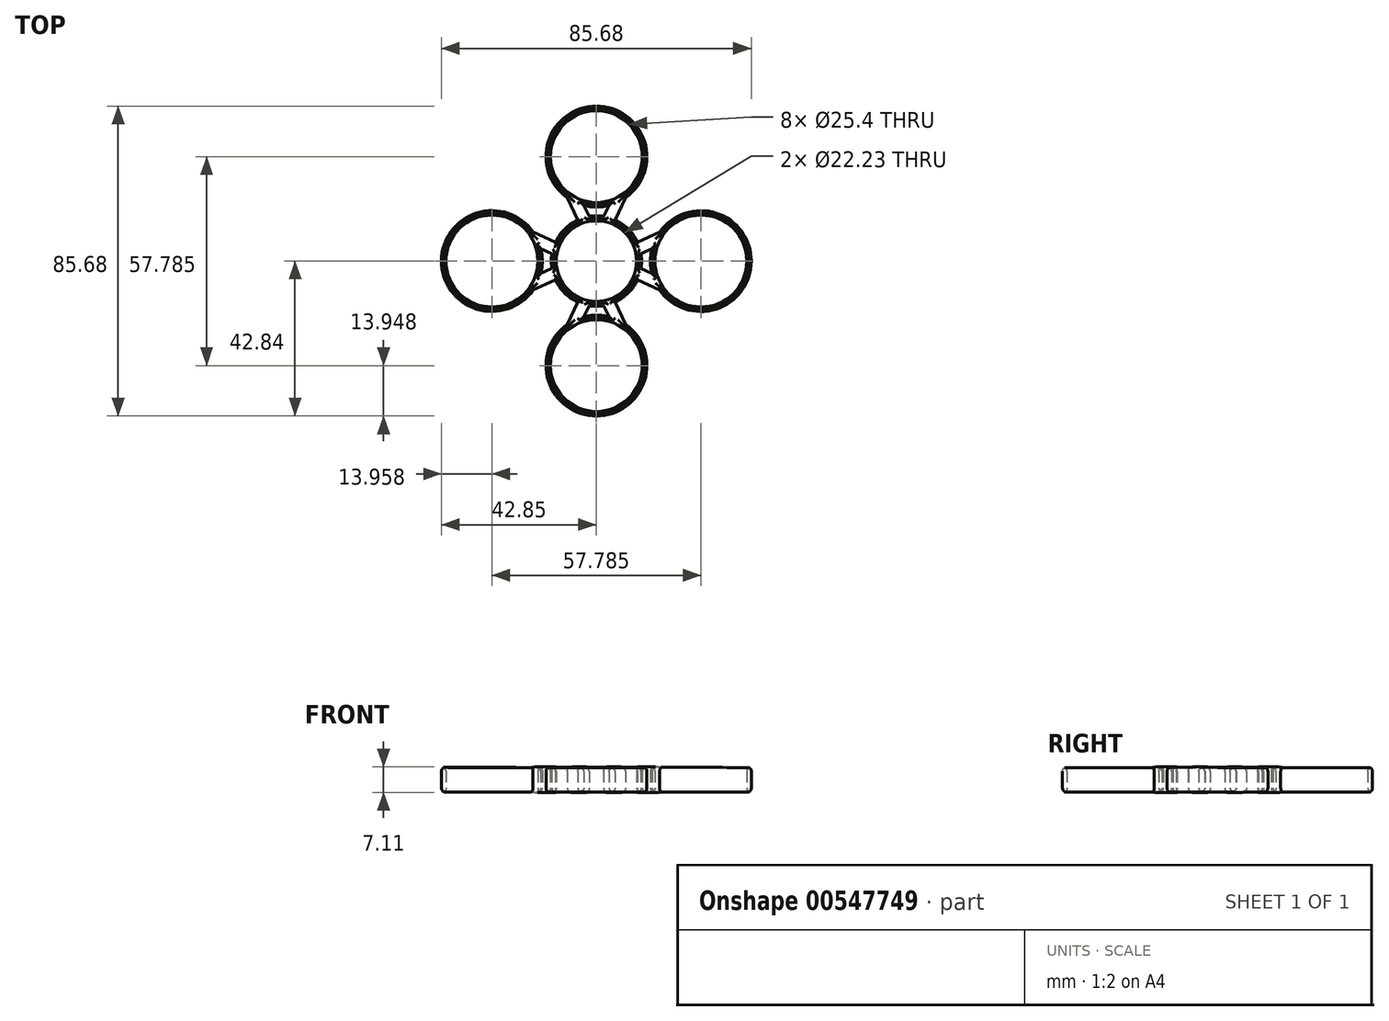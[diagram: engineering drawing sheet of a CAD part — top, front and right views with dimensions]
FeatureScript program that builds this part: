
annotation { "Feature Type Name" : "Feature", "Feature Type Description" : "" }
export const myFeature = defineFeature(function(context is Context, id is Id, definition is map)
    precondition{}
    {
        {
            var Q0;
            Q0=qCreatedBy(makeId("Top.planeOp"),FACE);
            var sketch = newSketch(context, id + "F0", { "sketchPlane" : qUnion([Q0])});
            skCircle(sketch, "E0", {"center": v(0, 0) * mm, "radius": 11.11 * mm});
            skCircle(sketch, "E1", {"center": v(0, 28.9) * mm, "radius": 12.7 * mm});
            skCircle(sketch, "E2", {"center": v(-28.9, 0) * mm, "radius": 12.7 * mm});
            skCircle(sketch, "E3", {"center": v(0, -28.9) * mm, "radius": 12.7 * mm});
            skCircle(sketch, "E4", {"center": v(28.9, 0) * mm, "radius": 12.7 * mm});
            skLineSegment(sketch, "E5", {"start": v(-8.04, 17.49) * mm, "end": v(-5.16, 11.36) * mm});
            skLineSegment(sketch, "E6", {"start": v(-3.46, 15.38) * mm, "end": v(-2.02, 12.31) * mm});
            skLineSegment(sketch, "E7.MirrorCS", {"start": v(3.46, 15.38) * mm, "end": v(2.02, 12.31) * mm});
            skLineSegment(sketch, "E8.MirrorCS", {"start": v(8.04, 17.49) * mm, "end": v(5.16, 11.36) * mm});
            skLineSegment(sketch, "E9.MirrorCS", {"start": v(8.04, -17.49) * mm, "end": v(5.16, -11.36) * mm});
            skLineSegment(sketch, "E10.MirrorCS", {"start": v(3.46, -15.38) * mm, "end": v(2.02, -12.31) * mm});
            skLineSegment(sketch, "E11.MirrorCS", {"start": v(-3.46, -15.38) * mm, "end": v(-2.02, -12.31) * mm});
            skLineSegment(sketch, "E12.MirrorCS", {"start": v(-8.04, -17.49) * mm, "end": v(-5.16, -11.36) * mm});
            skLineSegment(sketch, "E13.MirrorCS", {"start": v(17.5, 8.06) * mm, "end": v(11.36, 5.18) * mm});
            skLineSegment(sketch, "E14.MirrorCS", {"start": v(15.38, 3.47) * mm, "end": v(12.31, 2.04) * mm});
            skLineSegment(sketch, "E15.MirrorCS", {"start": v(15.36, -3.45) * mm, "end": v(12.31, -2.02) * mm});
            skLineSegment(sketch, "E16.MirrorCS", {"start": v(17.46, -8.02) * mm, "end": v(11.36, -5.16) * mm});
            skLineSegment(sketch, "E17.MirrorCS", {"start": v(-20.31, 9.35) * mm, "end": v(-20.27, 9.33) * mm});
            skLineSegment(sketch, "E18.MirrorCS", {"start": v(-16.9, 4.16) * mm, "end": v(-16.9, 4.16) * mm});
            skLineSegment(sketch, "E19.MirrorCS", {"start": v(-16.9, -4.18) * mm, "end": v(-16.9, -4.18) * mm});
            skLineSegment(sketch, "E20.MirrorCS", {"start": v(-20.31, -9.36) * mm, "end": v(-20.3, -9.36) * mm});
            skLineSegment(sketch, "E21", {"start": v(16.89, 4.18) * mm, "end": v(16.9, 4.2) * mm});
            skLineSegment(sketch, "E22", {"start": v(20.3, 9.36) * mm, "end": v(20.36, 9.4) * mm});
            skLineSegment(sketch, "E23", {"start": v(16.89, -4.16) * mm, "end": v(16.9, -4.17) * mm});
            skLineSegment(sketch, "E24", {"start": v(20.29, -9.34) * mm, "end": v(20.32, -9.37) * mm});
            skLineSegment(sketch, "E25", {"start": v(-10.13, 4.57) * mm, "end": v(-10.13, 4.57) * mm});
            skLineSegment(sketch, "E26", {"start": v(-11.03, 1.4) * mm, "end": v(-11.02, 1.4) * mm});
            skLineSegment(sketch, "E27", {"start": v(-11.03, -1.43) * mm, "end": v(-11.02, -1.42) * mm});
            skLineSegment(sketch, "E28", {"start": v(-10.13, -4.6) * mm, "end": v(-10.12, -4.58) * mm});
            skArc(sketch, "E29", {"start": v(-3.46, 15.38) * mm, "mid": v(0, 14.94) * mm, "end": v(3.46, 15.38) * mm});
            skArc(sketch, "E30.MirrorC", {"start": v(-3.46, -15.38) * mm, "mid": v(0, -14.94) * mm, "end": v(3.46, -15.38) * mm});
            skArc(sketch, "E31.MirrorC", {"start": v(-15.4, -3.47) * mm, "mid": v(-14.95, -0.01) * mm, "end": v(-15.38, 3.45) * mm});
            skArc(sketch, "E32.MirrorC", {"start": v(15.38, 3.47) * mm, "mid": v(14.93, 0.01) * mm, "end": v(15.36, -3.45) * mm});
            skPoint(sketch, "E33.orphan", {"position": v(-9.35, 20.3) * mm});
            skPoint(sketch, "E34.orphan", {"position": v(-4.17, 16.9) * mm});
            skPoint(sketch, "E35.orphan", {"position": v(4.17, 16.9) * mm});
            skPoint(sketch, "E36.orphan", {"position": v(9.35, 20.3) * mm});
            skLineSegment(sketch, "E37.trimOffspring", {"start": v(-17.48, 8.02) * mm, "end": v(-11.37, 5.15) * mm});
            skLineSegment(sketch, "E38.trimOffspring", {"start": v(-15.38, 3.45) * mm, "end": v(-12.32, 2.01) * mm});
            skLineSegment(sketch, "E39.trimOffspring", {"start": v(-15.4, -3.47) * mm, "end": v(-12.31, -2.03) * mm});
            skLineSegment(sketch, "E40.trimOffspring", {"start": v(-17.52, -8.06) * mm, "end": v(-11.36, -5.17) * mm});
            skArc(sketch, "E41.trimOffspring", {"start": v(-17.48, 8.02) * mm, "mid": v(-42.85, 0.05) * mm, "end": v(-17.52, -8.06) * mm});
            skArc(sketch, "E42.trimOffspring", {"start": v(8.04, 17.49) * mm, "mid": v(0, 42.84) * mm, "end": v(-8.04, 17.49) * mm});
            skArc(sketch, "E43.trimOffspring", {"start": v(17.46, -8.02) * mm, "mid": v(42.83, -0.05) * mm, "end": v(17.5, 8.06) * mm});
            skPoint(sketch, "E44.orphan", {"position": v(-9.35, -20.3) * mm});
            skPoint(sketch, "E45.orphan", {"position": v(-4.17, -16.9) * mm});
            skArc(sketch, "E46.trimOffspring", {"start": v(8.04, -17.49) * mm, "mid": v(0, -42.84) * mm, "end": v(-8.04, -17.49) * mm});
            skPoint(sketch, "E47.orphan", {"position": v(4.17, -16.9) * mm});
            skPoint(sketch, "E48.orphan", {"position": v(9.35, -20.3) * mm});
            skArc(sketch, "E49", {"start": v(-5.16, 11.36) * mm, "mid": v(-8.83, 8.82) * mm, "end": v(-11.37, 5.15) * mm});
            skPoint(sketch, "E50.orphan", {"position": v(-4.58, 10.12) * mm});
            skPoint(sketch, "E51.orphan", {"position": v(-1.42, 11.02) * mm});
            skArc(sketch, "E52.trimOffspring", {"start": v(2.02, 12.31) * mm, "mid": v(0, 12.48) * mm, "end": v(-2.02, 12.31) * mm});
            skPoint(sketch, "E53.orphan", {"position": v(1.42, 11.02) * mm});
            skPoint(sketch, "E54.orphan", {"position": v(4.58, 10.12) * mm});
            skArc(sketch, "E55.trimOffspring", {"start": v(-12.32, 2.01) * mm, "mid": v(-12.48, 0) * mm, "end": v(-12.31, -2.03) * mm});
            skArc(sketch, "E56.trimOffspring", {"start": v(-11.36, -5.17) * mm, "mid": v(-8.82, -8.83) * mm, "end": v(-5.16, -11.36) * mm});
            skPoint(sketch, "E57.orphan", {"position": v(-4.58, -10.12) * mm});
            skPoint(sketch, "E58.orphan", {"position": v(-1.42, -11.02) * mm});
            skArc(sketch, "E59.trimOffspring", {"start": v(-2.02, -12.31) * mm, "mid": v(0, -12.48) * mm, "end": v(2.02, -12.31) * mm});
            skPoint(sketch, "E60.orphan", {"position": v(1.42, -11.02) * mm});
            skArc(sketch, "E61.trimOffspring", {"start": v(5.16, -11.36) * mm, "mid": v(8.83, -8.82) * mm, "end": v(11.36, -5.16) * mm});
            skPoint(sketch, "E62.orphan", {"position": v(4.58, -10.12) * mm});
            skArc(sketch, "E63.trimOffspring", {"start": v(12.31, -2.02) * mm, "mid": v(12.48, 0) * mm, "end": v(12.31, 2.04) * mm});
            skLineSegment(sketch, "E64.trimOffspring", {"start": v(11.02, -1.41) * mm, "end": v(11.01, -1.4) * mm});
            skLineSegment(sketch, "E65.trimOffspring", {"start": v(10.13, -4.58) * mm, "end": v(10.11, -4.57) * mm});
            skLineSegment(sketch, "E66.trimOffspring", {"start": v(11.02, 1.43) * mm, "end": v(11.01, 1.43) * mm});
            skLineSegment(sketch, "E67.trimOffspring", {"start": v(10.12, 4.6) * mm, "end": v(10.11, 4.6) * mm});
            skArc(sketch, "E68.trimOffspring", {"start": v(11.36, 5.18) * mm, "mid": v(8.82, 8.83) * mm, "end": v(5.16, 11.36) * mm});
            skLineSegment(sketch, "E69.trimOffspring", {"start": v(0, 0.01) * mm, "end": v(0, 0) * mm});
            skLineSegment(sketch, "E70.trimOffspring", {"start": v(-0.01, 0) * mm, "end": v(0, 0) * mm});
            skLineSegment(sketch, "E71.trimOffspring", {"start": v(-0.01, 0) * mm, "end": v(-0.01, 0) * mm});
            skLineSegment(sketch, "E72.trimOffspring", {"start": v(0, 0) * mm, "end": v(-0.01, 0) * mm});
            skSolve(sketch);
        }
        {
            var Q0;
            Q0=makeQuery(id+"F0.imprint","IMPRINT",FACE,{"disambiguationData":[TD([[makeQuery(id+"F0.imprint","IMPRINT",EDGE,{"derivedFrom":sQuery(id+"F0.wireOp",EDGE,"E1")}),-1.0]])]});
            extrude(context, id + "F1", {"entities" : qUnion([Q0]), "depth" : 7.11 * mm, "offsetDistance" : 25.4 * mm});
        }
        {
            var Q0;
            Q0=makeQuery(id+"F1.opExtrude","CAP_FACE",FACE,{"disambiguationData":[OSD([sQuery(id+"F0.wireOp",EDGE,"E0"),sQuery(id+"F0.wireOp",EDGE,"E1"),sQuery(id+"F0.wireOp",EDGE,"E2"),sQuery(id+"F0.wireOp",EDGE,"E3"),sQuery(id+"F0.wireOp",EDGE,"E4"),sQuery(id+"F0.wireOp",EDGE,"E5"),sQuery(id+"F0.wireOp",EDGE,"E6"),sQuery(id+"F0.wireOp",EDGE,"E7.MirrorCS"),sQuery(id+"F0.wireOp",EDGE,"E8.MirrorCS"),sQuery(id+"F0.wireOp",EDGE,"E9.MirrorCS"),sQuery(id+"F0.wireOp",EDGE,"E10.MirrorCS"),sQuery(id+"F0.wireOp",EDGE,"E11.MirrorCS"),sQuery(id+"F0.wireOp",EDGE,"E12.MirrorCS"),sQuery(id+"F0.wireOp",EDGE,"E13.MirrorCS"),sQuery(id+"F0.wireOp",EDGE,"E14.MirrorCS"),sQuery(id+"F0.wireOp",EDGE,"E15.MirrorCS"),sQuery(id+"F0.wireOp",EDGE,"E16.MirrorCS"),sQuery(id+"F0.wireOp",EDGE,"E29"),sQuery(id+"F0.wireOp",EDGE,"E30.MirrorC"),sQuery(id+"F0.wireOp",EDGE,"E31.MirrorC"),sQuery(id+"F0.wireOp",EDGE,"E32.MirrorC"),sQuery(id+"F0.wireOp",EDGE,"E37.trimOffspring"),sQuery(id+"F0.wireOp",EDGE,"E38.trimOffspring"),sQuery(id+"F0.wireOp",EDGE,"E39.trimOffspring"),sQuery(id+"F0.wireOp",EDGE,"E40.trimOffspring"),sQuery(id+"F0.wireOp",EDGE,"E41.trimOffspring"),sQuery(id+"F0.wireOp",EDGE,"E42.trimOffspring"),sQuery(id+"F0.wireOp",EDGE,"E43.trimOffspring"),sQuery(id+"F0.wireOp",EDGE,"E46.trimOffspring"),sQuery(id+"F0.wireOp",EDGE,"E49"),sQuery(id+"F0.wireOp",EDGE,"E52.trimOffspring"),sQuery(id+"F0.wireOp",EDGE,"E55.trimOffspring"),sQuery(id+"F0.wireOp",EDGE,"E56.trimOffspring"),sQuery(id+"F0.wireOp",EDGE,"E59.trimOffspring"),sQuery(id+"F0.wireOp",EDGE,"E61.trimOffspring"),sQuery(id+"F0.wireOp",EDGE,"E63.trimOffspring"),sQuery(id+"F0.wireOp",EDGE,"E68.trimOffspring")])],"isStart":false});
            var Q1;
            Q1=makeQuery(id+"F1.opExtrude","CAP_FACE",FACE,{"disambiguationData":[OSD([sQuery(id+"F0.wireOp",EDGE,"E0"),sQuery(id+"F0.wireOp",EDGE,"E1"),sQuery(id+"F0.wireOp",EDGE,"E2"),sQuery(id+"F0.wireOp",EDGE,"E3"),sQuery(id+"F0.wireOp",EDGE,"E4"),sQuery(id+"F0.wireOp",EDGE,"E5"),sQuery(id+"F0.wireOp",EDGE,"E6"),sQuery(id+"F0.wireOp",EDGE,"E7.MirrorCS"),sQuery(id+"F0.wireOp",EDGE,"E8.MirrorCS"),sQuery(id+"F0.wireOp",EDGE,"E9.MirrorCS"),sQuery(id+"F0.wireOp",EDGE,"E10.MirrorCS"),sQuery(id+"F0.wireOp",EDGE,"E11.MirrorCS"),sQuery(id+"F0.wireOp",EDGE,"E12.MirrorCS"),sQuery(id+"F0.wireOp",EDGE,"E13.MirrorCS"),sQuery(id+"F0.wireOp",EDGE,"E14.MirrorCS"),sQuery(id+"F0.wireOp",EDGE,"E15.MirrorCS"),sQuery(id+"F0.wireOp",EDGE,"E16.MirrorCS"),sQuery(id+"F0.wireOp",EDGE,"E29"),sQuery(id+"F0.wireOp",EDGE,"E30.MirrorC"),sQuery(id+"F0.wireOp",EDGE,"E31.MirrorC"),sQuery(id+"F0.wireOp",EDGE,"E32.MirrorC"),sQuery(id+"F0.wireOp",EDGE,"E37.trimOffspring"),sQuery(id+"F0.wireOp",EDGE,"E38.trimOffspring"),sQuery(id+"F0.wireOp",EDGE,"E39.trimOffspring"),sQuery(id+"F0.wireOp",EDGE,"E40.trimOffspring"),sQuery(id+"F0.wireOp",EDGE,"E41.trimOffspring"),sQuery(id+"F0.wireOp",EDGE,"E42.trimOffspring"),sQuery(id+"F0.wireOp",EDGE,"E43.trimOffspring"),sQuery(id+"F0.wireOp",EDGE,"E46.trimOffspring"),sQuery(id+"F0.wireOp",EDGE,"E49"),sQuery(id+"F0.wireOp",EDGE,"E52.trimOffspring"),sQuery(id+"F0.wireOp",EDGE,"E55.trimOffspring"),sQuery(id+"F0.wireOp",EDGE,"E56.trimOffspring"),sQuery(id+"F0.wireOp",EDGE,"E59.trimOffspring"),sQuery(id+"F0.wireOp",EDGE,"E61.trimOffspring"),sQuery(id+"F0.wireOp",EDGE,"E63.trimOffspring"),sQuery(id+"F0.wireOp",EDGE,"E68.trimOffspring")])],"isStart":true});
            fillet(context, id + "F2", {"entities" : qUnion([Q0, Q1]), "radius" : 1.27 * mm, "tangentPropagation" : true, "allowEdgeOverflow" : false});
        }
    });
